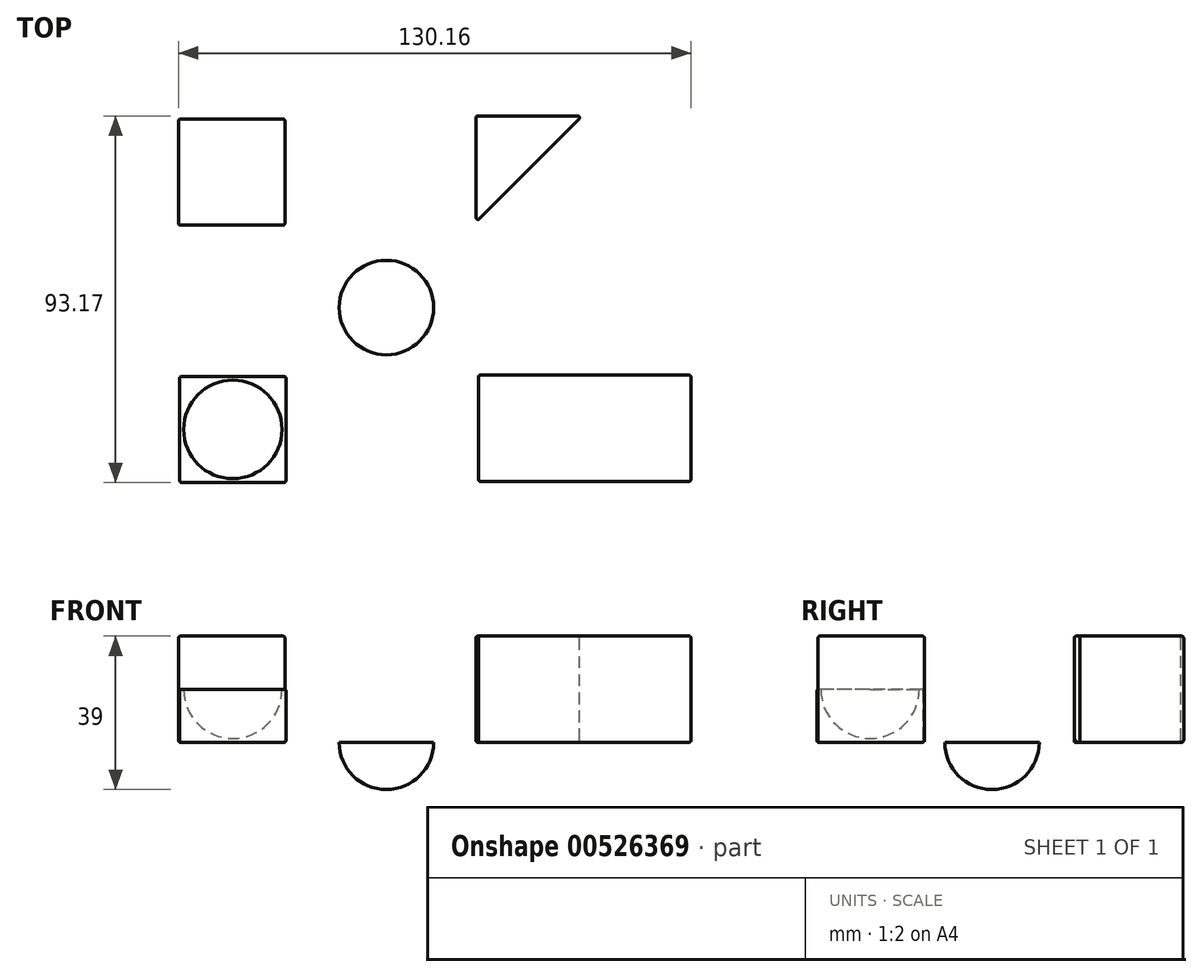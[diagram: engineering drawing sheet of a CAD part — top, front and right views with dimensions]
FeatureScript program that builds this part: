
annotation { "Feature Type Name" : "Feature", "Feature Type Description" : "" }
export const myFeature = defineFeature(function(context is Context, id is Id, definition is map)
    precondition{}
    {
        {
            var Q0;
            Q0=qCreatedBy(makeId("Top.planeOp"),FACE);
            var sketch = newSketch(context, id + "F0", { "sketchPlane" : qUnion([Q0])});
            skLineSegment(sketch, "E0.bottom", {"start": v(-52.78, 47.9) * mm, "end": v(-25.78, 47.9) * mm});
            skLineSegment(sketch, "E0.top", {"start": v(-52.78, 20.9) * mm, "end": v(-25.78, 20.9) * mm});
            skLineSegment(sketch, "E0.left", {"start": v(-52.78, 47.9) * mm, "end": v(-52.78, 20.9) * mm});
            skLineSegment(sketch, "E0.right", {"start": v(-25.78, 47.9) * mm, "end": v(-25.78, 20.9) * mm});
            skLineSegment(sketch, "E1.bottom", {"start": v(22.79, 48.7) * mm, "end": v(49.79, 48.7) * mm});
            skLineSegment(sketch, "E1.top", {"start": v(22.79, 21.7) * mm, "end": v(49.79, 21.7) * mm});
            skLineSegment(sketch, "E1.left", {"start": v(22.79, 48.7) * mm, "end": v(22.79, 21.7) * mm});
            skLineSegment(sketch, "E1.right", {"start": v(49.79, 48.7) * mm, "end": v(49.79, 21.7) * mm});
            skLineSegment(sketch, "E2.bottom", {"start": v(23.38, -17.18) * mm, "end": v(77.38, -17.18) * mm});
            skLineSegment(sketch, "E2.top", {"start": v(23.38, -44.18) * mm, "end": v(77.38, -44.18) * mm});
            skLineSegment(sketch, "E2.left", {"start": v(23.38, -17.18) * mm, "end": v(23.38, -44.18) * mm});
            skLineSegment(sketch, "E2.right", {"start": v(77.38, -17.18) * mm, "end": v(77.38, -44.18) * mm});
            skLineSegment(sketch, "E3.bottom", {"start": v(-52.5, -17.48) * mm, "end": v(-25.5, -17.48) * mm});
            skLineSegment(sketch, "E3.top", {"start": v(-52.5, -44.48) * mm, "end": v(-25.5, -44.48) * mm});
            skLineSegment(sketch, "E3.left", {"start": v(-52.5, -17.48) * mm, "end": v(-52.5, -44.48) * mm});
            skLineSegment(sketch, "E3.right", {"start": v(-25.5, -17.48) * mm, "end": v(-25.5, -44.48) * mm});
            skLineSegment(sketch, "E4", {"start": v(22.79, 21.7) * mm, "end": v(49.79, 48.7) * mm});
            skSolve(sketch);
        }
        {
            var Q0;
            Q0=makeQuery(id+"F0.imprint","IMPRINT",FACE,{"disambiguationData":[TD([[makeQuery(id+"F0.imprint","IMPRINT",EDGE,{"derivedFrom":sQuery(id+"F0.wireOp",EDGE,"E0.bottom")}),-1.0]])]});
            extrude(context, id + "F1", {"entities" : qUnion([Q0]), "depth" : 27 * mm, "offsetDistance" : 25 * mm});
        }
        {
            var Q0;
            Q0=makeQuery(id+"F0.imprint","IMPRINT",FACE,{"disambiguationData":[TD([[makeQuery(id+"F0.imprint","IMPRINT",EDGE,{"derivedFrom":sQuery(id+"F0.wireOp",EDGE,"E1.bottom")}),-1.0]])]});
            extrude(context, id + "F2", {"entities" : qUnion([Q0]), "depth" : 27 * mm, "offsetDistance" : 25 * mm});
        }
        {
            var Q0;
            Q0=makeQuery(id+"F0.imprint","IMPRINT",FACE,{"disambiguationData":[TD([[makeQuery(id+"F0.imprint","IMPRINT",EDGE,{"derivedFrom":sQuery(id+"F0.wireOp",EDGE,"E3.bottom")}),-1.0]])]});
            extrude(context, id + "F3", {"entities" : qUnion([Q0]), "depth" : 13.5 * mm, "offsetDistance" : 25 * mm});
        }
        {
            var Q0;
            Q0=makeQuery(id+"F3.opExtrude","CAP_FACE",FACE,{"disambiguationData":[OSD([sQuery(id+"F0.wireOp",EDGE,"E3.bottom"),sQuery(id+"F0.wireOp",EDGE,"E3.top"),sQuery(id+"F0.wireOp",EDGE,"E3.left"),sQuery(id+"F0.wireOp",EDGE,"E3.right")])],"isStart":false});
            var sketch = newSketch(context, id + "F4", { "sketchPlane" : qUnion([Q0])});
            skCircle(sketch, "E5", {"center": v(-39, -30.98) * mm, "radius": 12.5 * mm});
            skPoint(sketch, "E5.centerSnap0", {"position": v(-52.5, -30.98) * mm});
            skPoint(sketch, "E5.centerSnap1", {"position": v(-39, -17.48) * mm});
            skLineSegment(sketch, "E6", {"start": v(-52.5, -30.98) * mm, "end": v(-25.5, -30.98) * mm});
            skSolve(sketch);
        }
        {
            var Q0;
            {var subQ0=sQuery(id+"F4.wireOp",EDGE,"E6");var subQ1=sQuery(id+"F4.wireOp",EDGE,"E5");var subQ2=makeQuery(id+"F4.imprint","INTERSECT",VERTEX,{"disambiguationData":[OD(0.0)],"derivedFrom":[subQ1,subQ0]});Q0=makeQuery(id+"F4.imprint","IMPRINT",FACE,{"disambiguationData":[TD([[makeQuery(id+"F4.imprint","IMPRINT",EDGE,{"disambiguationData":[TD([[subQ2,1.0]])],"derivedFrom":subQ1}),1.0]])]});}
            var Q1;
            Q1=sQuery(id+"F4.wireOp",EDGE,"E6");
            revolve(context, id + "F5", {"operationType" : NewBodyOperationType.REMOVE, "entities" : qUnion([Q0]), "axis" : qUnion([Q1]), "revolveType" : RevolveType.FULL, "oppositeDirection" : true});
        }
        {
            var Q0;
            Q0=qCreatedBy(makeId("Top.planeOp"),FACE);
            var sketch = newSketch(context, id + "F6", { "sketchPlane" : qUnion([Q0])});
            skCircle(sketch, "E7", {"center": v(0, 0) * mm, "radius": 12 * mm});
            skLineSegment(sketch, "E8", {"start": v(-17.6, 0) * mm, "end": v(19.22, 0) * mm});
            skSolve(sketch);
        }
        {
            var Q0;
            {var subQ0=sQuery(id+"F6.wireOp",EDGE,"E8");var subQ1=sQuery(id+"F6.wireOp",EDGE,"E7");var subQ2=makeQuery(id+"F6.imprint","INTERSECT",VERTEX,{"disambiguationData":[OD(0.0)],"derivedFrom":[subQ1,subQ0]});Q0=makeQuery(id+"F6.imprint","IMPRINT",FACE,{"disambiguationData":[TD([[makeQuery(id+"F6.imprint","IMPRINT",EDGE,{"disambiguationData":[TD([[subQ2,1.0]])],"derivedFrom":subQ1}),1.0]])]});}
            var Q1;
            Q1=sQuery(id+"F6.wireOp",EDGE,"E8");
            revolve(context, id + "F7", {"entities" : qUnion([Q0]), "axis" : qUnion([Q1]), "revolveType" : RevolveType.ONE_DIRECTION, "angle" : 180 * degree});
        }
        {
            var Q0;
            Q0=makeQuery(id+"F0.imprint","IMPRINT",FACE,{"disambiguationData":[TD([[makeQuery(id+"F0.imprint","IMPRINT",EDGE,{"derivedFrom":sQuery(id+"F0.wireOp",EDGE,"E2.bottom")}),-1.0]])]});
            extrude(context, id + "F8", {"entities" : qUnion([Q0]), "depth" : 27 * mm, "offsetDistance" : 25 * mm});
        }
        {
            var Q0;
            Q0=makeQuery(id+"F1.opExtrude","CAP_FACE",FACE,{"disambiguationData":[OSD([sQuery(id+"F0.wireOp",EDGE,"E0.bottom"),sQuery(id+"F0.wireOp",EDGE,"E0.top"),sQuery(id+"F0.wireOp",EDGE,"E0.left"),sQuery(id+"F0.wireOp",EDGE,"E0.right")])],"isStart":false});
            var Q1;
            Q1=makeQuery(id+"F1.opExtrude","SWEPT_FACE",FACE,{"disambiguationData":[OSD([sQuery(id+"F0.wireOp",EDGE,"E0.bottom")])]});
            var Q2;
            Q2=makeQuery(id+"F1.opExtrude","SWEPT_FACE",FACE,{"disambiguationData":[OSD([sQuery(id+"F0.wireOp",EDGE,"E0.left")])]});
            var Q3;
            Q3=makeQuery(id+"F1.opExtrude","SWEPT_FACE",FACE,{"disambiguationData":[OSD([sQuery(id+"F0.wireOp",EDGE,"E0.right")])]});
            var Q4;
            Q4=makeQuery(id+"F2.opExtrude","SWEPT_FACE",FACE,{"disambiguationData":[OSD([sQuery(id+"F0.wireOp",EDGE,"E4")])]});
            fillet(context, id + "F9", {"entities" : qUnion([Q0, Q1, Q2, Q3, Q4]), "radius" : 0.5 * mm, "tangentPropagation" : true, "allowEdgeOverflow" : false});
        }
        {
            var Q0;
            Q0=makeQuery(id+"F2.opExtrude","CAP_FACE",FACE,{"disambiguationData":[OSD([sQuery(id+"F0.wireOp",EDGE,"E1.bottom"),sQuery(id+"F0.wireOp",EDGE,"E1.left"),sQuery(id+"F0.wireOp",EDGE,"E4")])],"isStart":true});
            var Q1;
            Q1=makeQuery(id+"F2.opExtrude","SWEPT_FACE",FACE,{"disambiguationData":[OSD([sQuery(id+"F0.wireOp",EDGE,"E4")])]});
            var Q2;
            Q2=makeQuery(id+"F2.opExtrude","SWEPT_FACE",FACE,{"disambiguationData":[OSD([sQuery(id+"F0.wireOp",EDGE,"E1.bottom")])]});
            var Q3;
            Q3=makeQuery(id+"F2.opExtrude","SWEPT_FACE",FACE,{"disambiguationData":[OSD([sQuery(id+"F0.wireOp",EDGE,"E1.left")])]});
            var Q4;
            {var subQ0=sQuery(id+"F0.wireOp",EDGE,"E4");Q4=makeQuery(id+"F9.opFillet","BLEND_EDGE",EDGE,{"blendedFrom":[makeQuery(id+"F2.opExtrude","CAP_EDGE",EDGE,{"disambiguationData":[OSD([subQ0])],"isStart":false}),makeQuery(id+"F2.opExtrude","SWEPT_FACE",FACE,{"disambiguationData":[OSD([subQ0])]})],"blendedInto":[makeQuery(id+"F2.opExtrude","SWEPT_FACE",FACE,{"disambiguationData":[OSD([subQ0])]})]});}
            var Q5;
            {var subQ0=sQuery(id+"F0.wireOp",EDGE,"E4");Q5=makeQuery(id+"F9.opFillet","BLEND_EDGE",EDGE,{"blendedFrom":[makeQuery(id+"F2.opExtrude","CAP_EDGE",EDGE,{"disambiguationData":[OSD([subQ0])],"isStart":false}),makeQuery(id+"F2.opExtrude","CAP_FACE",FACE,{"disambiguationData":[OSD([sQuery(id+"F0.wireOp",EDGE,"E1.bottom"),sQuery(id+"F0.wireOp",EDGE,"E1.left"),subQ0])],"isStart":false})],"blendedInto":[makeQuery(id+"F2.opExtrude","CAP_FACE",FACE,{"disambiguationData":[OSD([sQuery(id+"F0.wireOp",EDGE,"E1.bottom"),sQuery(id+"F0.wireOp",EDGE,"E1.left"),subQ0])],"isStart":false})]});}
            fillet(context, id + "F10", {"entities" : qUnion([Q0, Q1, Q2, Q3, Q4, Q5]), "radius" : 0.5 * mm, "tangentPropagation" : true, "allowEdgeOverflow" : false});
        }
        {
            var Q0;
            Q0=makeQuery(id+"F3.opExtrude","CAP_FACE",FACE,{"disambiguationData":[OSD([sQuery(id+"F0.wireOp",EDGE,"E3.bottom"),sQuery(id+"F0.wireOp",EDGE,"E3.top"),sQuery(id+"F0.wireOp",EDGE,"E3.left"),sQuery(id+"F0.wireOp",EDGE,"E3.right")])],"isStart":true});
            var Q1;
            Q1=makeQuery(id+"F3.opExtrude","SWEPT_FACE",FACE,{"disambiguationData":[OSD([sQuery(id+"F0.wireOp",EDGE,"E3.left")])]});
            var Q2;
            Q2=makeQuery(id+"F3.opExtrude","SWEPT_FACE",FACE,{"disambiguationData":[OSD([sQuery(id+"F0.wireOp",EDGE,"E3.top")])]});
            var Q3;
            Q3=makeQuery(id+"F3.opExtrude","SWEPT_FACE",FACE,{"disambiguationData":[OSD([sQuery(id+"F0.wireOp",EDGE,"E3.right")])]});
            var Q4;
            Q4=makeQuery(id+"F3.opExtrude","SWEPT_FACE",FACE,{"disambiguationData":[OSD([sQuery(id+"F0.wireOp",EDGE,"E3.bottom")])]});
            fillet(context, id + "F11", {"entities" : qUnion([Q0, Q1, Q2, Q3, Q4]), "radius" : 0.5 * mm, "tangentPropagation" : true, "allowEdgeOverflow" : false});
        }
        {
            var Q0;
            Q0=makeQuery(id+"F8.opExtrude","CAP_FACE",FACE,{"disambiguationData":[OSD([sQuery(id+"F0.wireOp",EDGE,"E2.bottom"),sQuery(id+"F0.wireOp",EDGE,"E2.top"),sQuery(id+"F0.wireOp",EDGE,"E2.left"),sQuery(id+"F0.wireOp",EDGE,"E2.right")])],"isStart":false});
            var Q1;
            Q1=makeQuery(id+"F8.opExtrude","SWEPT_FACE",FACE,{"disambiguationData":[OSD([sQuery(id+"F0.wireOp",EDGE,"E2.top")])]});
            var Q2;
            Q2=makeQuery(id+"F8.opExtrude","SWEPT_FACE",FACE,{"disambiguationData":[OSD([sQuery(id+"F0.wireOp",EDGE,"E2.left")])]});
            var Q3;
            Q3=makeQuery(id+"F8.opExtrude","SWEPT_FACE",FACE,{"disambiguationData":[OSD([sQuery(id+"F0.wireOp",EDGE,"E2.bottom")])]});
            var Q4;
            Q4=makeQuery(id+"F8.opExtrude","SWEPT_FACE",FACE,{"disambiguationData":[OSD([sQuery(id+"F0.wireOp",EDGE,"E2.right")])]});
            var Q5;
            Q5=makeQuery(id+"F8.opExtrude","CAP_FACE",FACE,{"disambiguationData":[OSD([sQuery(id+"F0.wireOp",EDGE,"E2.bottom"),sQuery(id+"F0.wireOp",EDGE,"E2.top"),sQuery(id+"F0.wireOp",EDGE,"E2.left"),sQuery(id+"F0.wireOp",EDGE,"E2.right")])],"isStart":true});
            fillet(context, id + "F12", {"entities" : qUnion([Q0, Q1, Q2, Q3, Q4, Q5]), "radius" : 0.5 * mm, "tangentPropagation" : true, "allowEdgeOverflow" : false});
        }
    });
